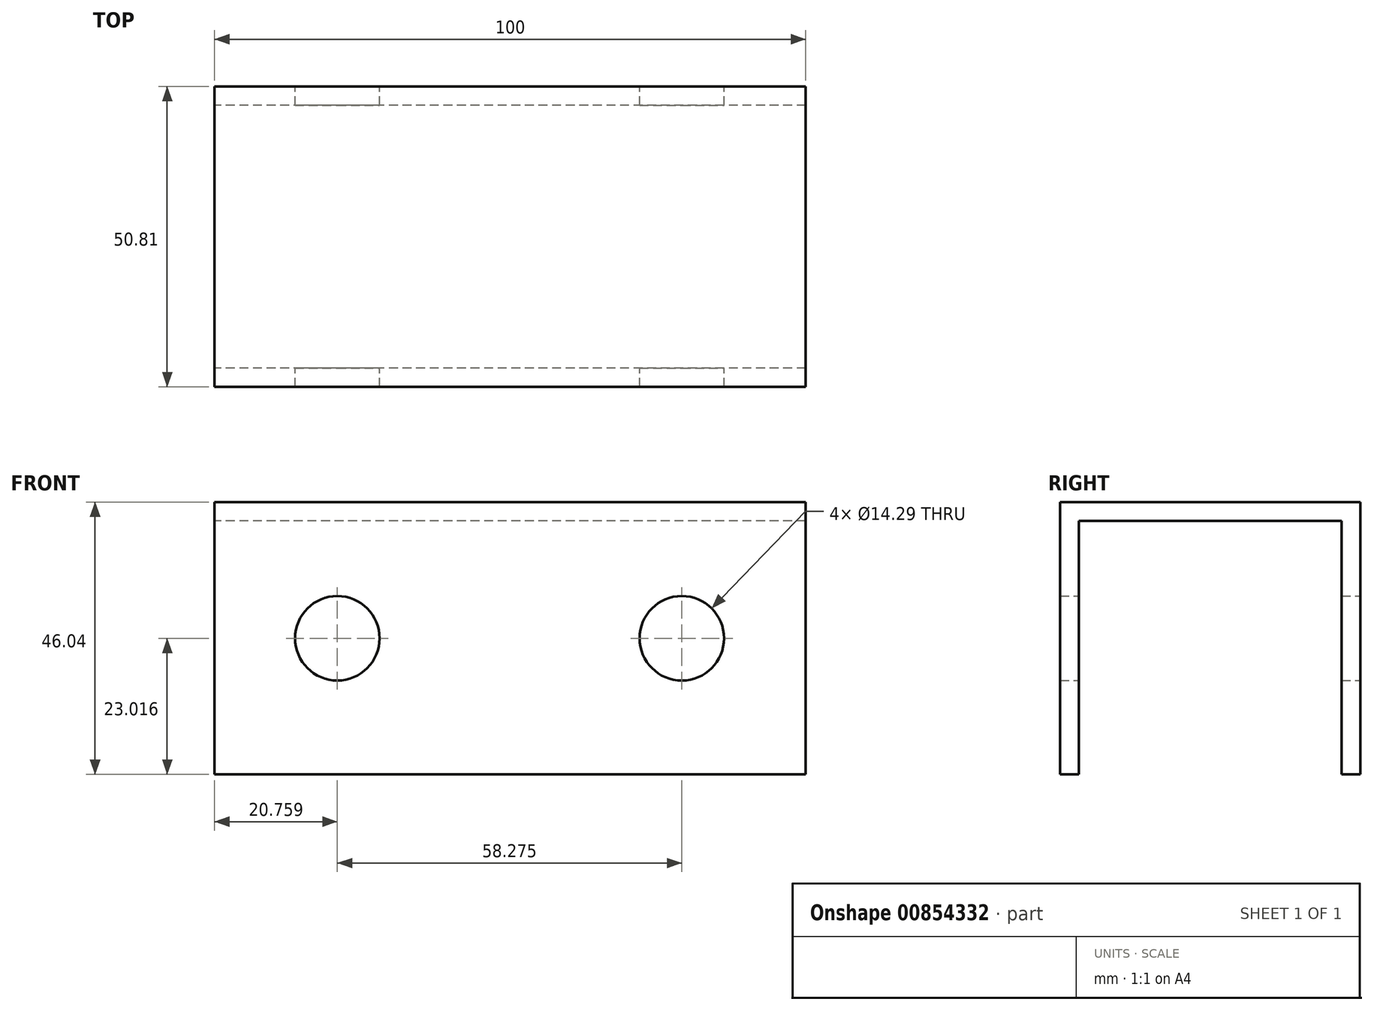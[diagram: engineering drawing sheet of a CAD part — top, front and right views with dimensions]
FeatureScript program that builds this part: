
annotation { "Feature Type Name" : "Feature", "Feature Type Description" : "" }
export const myFeature = defineFeature(function(context is Context, id is Id, definition is map)
    precondition{}
    {
        {
            var Q0;
            Q0=qCreatedBy(makeId("Right.planeOp"),FACE);
            var sketch = newSketch(context, id + "F0", { "sketchPlane" : qUnion([Q0])});
            skLineSegment(sketch, "E0.bottom", {"start": v(0, 0) * mm, "end": v(44.45, 0) * mm});
            skLineSegment(sketch, "E0.left", {"start": v(0, 0) * mm, "end": v(0, -42.86) * mm});
            skLineSegment(sketch, "E0.right", {"start": v(44.45, 0) * mm, "end": v(44.45, -42.86) * mm});
            skLineSegment(sketch, "E1.0", {"start": v(-3.18, 3.17) * mm, "end": v(-3.17, -42.86) * mm});
            skLineSegment(sketch, "E1.1", {"start": v(-3.17, 3.18) * mm, "end": v(47.62, 3.18) * mm});
            skLineSegment(sketch, "E1.2", {"start": v(47.62, 3.17) * mm, "end": v(47.62, -42.86) * mm});
            skLineSegment(sketch, "E2", {"start": v(0, -42.86) * mm, "end": v(-3.17, -42.86) * mm});
            skLineSegment(sketch, "E3", {"start": v(44.45, -42.86) * mm, "end": v(47.62, -42.86) * mm});
            skSolve(sketch);
        }
        {
            var Q0;
            Q0=makeQuery(id+"F0.imprint","IMPRINT",FACE,{"disambiguationData":[TD([[makeQuery(id+"F0.imprint","IMPRINT",EDGE,{"derivedFrom":sQuery(id+"F0.wireOp",EDGE,"E0.bottom")}),1.0]])]});
            extrude(context, id + "F1", {"entities" : qUnion([Q0]), "endBound" : BoundingType.SYMMETRIC, "depth" : 100 * mm, "offsetDistance" : 25 * mm});
        }
        {
            var Q0;
            Q0=makeQuery(id+"F1.opExtrude","SWEPT_FACE",FACE,{"disambiguationData":[OSD([sQuery(id+"F0.wireOp",EDGE,"E1.2")])]});
            var sketch = newSketch(context, id + "F2", { "sketchPlane" : qUnion([Q0])});
            skCircle(sketch, "E4", {"center": v(-29.03, -19.84) * mm, "radius": 7.14 * mm});
            skLineSegment(sketch, "E5", {"start": v(-29.03, -19.84) * mm, "end": v(29.24, -19.84) * mm, "construction": true});
            skCircle(sketch, "E6", {"center": v(29.24, -19.84) * mm, "radius": 7.14 * mm});
            skLineSegment(sketch, "E7", {"start": v(0, 3.17) * mm, "end": v(0, -19.84) * mm, "construction": true});
            skLineSegment(sketch, "E8", {"start": v(0, -19.84) * mm, "end": v(0, -42.86) * mm, "construction": true});
            skSolve(sketch);
        }
        {
            var Q0;
            Q0 = qSketchRegion(id + "F2", true);
            extrude(context, id + "F3", {"entities" : qUnion([Q0]), "operationType" : NewBodyOperationType.REMOVE, "endBound" : BoundingType.THROUGH_ALL, "oppositeDirection" : true, "depth" : 25 * mm, "offsetDistance" : 25 * mm});
        }
    });
